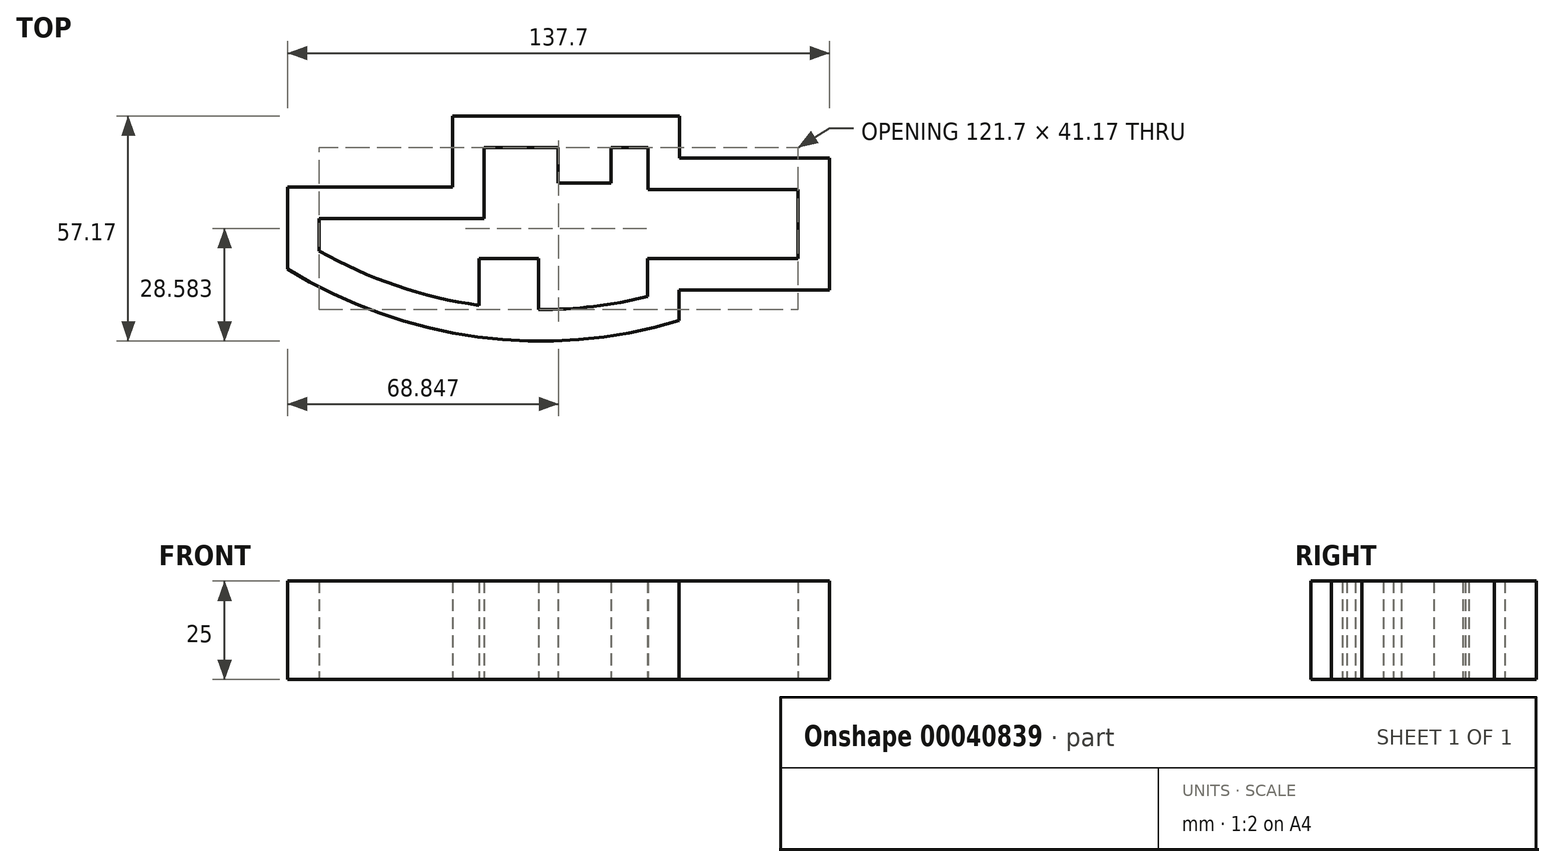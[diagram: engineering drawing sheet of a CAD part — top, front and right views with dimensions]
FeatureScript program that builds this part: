
annotation { "Feature Type Name" : "Feature", "Feature Type Description" : "" }
export const myFeature = defineFeature(function(context is Context, id is Id, definition is map)
    precondition{}
    {
        {
            var Q0;
            Q0=qCreatedBy(makeId("Top.planeOp"),FACE);
            var sketch = newSketch(context, id + "F0", { "sketchPlane" : qUnion([Q0])});
            skLineSegment(sketch, "E0", {"start": v(-50.92, 1.99) * mm, "end": v(-50.92, 10.24) * mm});
            skLineSegment(sketch, "E1", {"start": v(-50.92, 10.24) * mm, "end": v(-9.06, 10.24) * mm});
            skLineSegment(sketch, "E2", {"start": v(-9.06, 10.24) * mm, "end": v(-9.06, 28.27) * mm});
            skLineSegment(sketch, "E3", {"start": v(-9.06, 28.27) * mm, "end": v(9.73, 28.27) * mm});
            skLineSegment(sketch, "E4", {"start": v(32.61, 28.27) * mm, "end": v(32.61, 17.6) * mm});
            skLineSegment(sketch, "E5", {"start": v(32.61, 17.6) * mm, "end": v(70.78, 17.6) * mm});
            skLineSegment(sketch, "E6", {"start": v(70.78, 17.6) * mm, "end": v(70.78, 0) * mm});
            skLineSegment(sketch, "E7", {"start": v(70.78, 0) * mm, "end": v(32.48, 0) * mm});
            skLineSegment(sketch, "E8", {"start": v(32.48, 0) * mm, "end": v(32.48, -9.6) * mm});
            skArc(sketch, "E9", {"start": v(-50.92, 1.99) * mm, "mid": v(-31.29, -6.85) * mm, "end": v(-10.33, -11.82) * mm});
            skLineSegment(sketch, "E10.0", {"start": v(40.61, 36.27) * mm, "end": v(40.61, 25.6) * mm});
            skLineSegment(sketch, "E10.1", {"start": v(-17.06, 36.27) * mm, "end": v(40.61, 36.27) * mm});
            skLineSegment(sketch, "E10.2", {"start": v(40.61, 25.6) * mm, "end": v(78.78, 25.6) * mm});
            skLineSegment(sketch, "E10.3", {"start": v(-17.06, 18.24) * mm, "end": v(-17.06, 36.27) * mm});
            skLineSegment(sketch, "E10.4", {"start": v(-58.92, 18.24) * mm, "end": v(-17.06, 18.24) * mm});
            skLineSegment(sketch, "E10.5", {"start": v(-58.92, -2.56) * mm, "end": v(-58.92, 18.24) * mm});
            skLineSegment(sketch, "E10.6", {"start": v(78.78, 25.6) * mm, "end": v(78.78, -8) * mm});
            skLineSegment(sketch, "E10.7", {"start": v(78.78, -8) * mm, "end": v(40.48, -8) * mm});
            skLineSegment(sketch, "E10.8", {"start": v(40.48, -8) * mm, "end": v(40.48, -15.7) * mm});
            skArc(sketch, "E10.9", {"start": v(-58.92, -2.56) * mm, "mid": v(-10.64, -19.85) * mm, "end": v(40.48, -15.7) * mm});
            skLineSegment(sketch, "E11", {"start": v(9.73, 28.27) * mm, "end": v(9.73, 19.17) * mm});
            skLineSegment(sketch, "E12", {"start": v(9.73, 19.17) * mm, "end": v(23.3, 19.17) * mm});
            skLineSegment(sketch, "E13", {"start": v(23.3, 19.17) * mm, "end": v(23.3, 28.27) * mm});
            skLineSegment(sketch, "E14", {"start": v(-10.33, -11.82) * mm, "end": v(-10.33, 0) * mm});
            skLineSegment(sketch, "E15", {"start": v(-10.33, 0) * mm, "end": v(4.88, 0) * mm});
            skLineSegment(sketch, "E16", {"start": v(4.88, 0) * mm, "end": v(4.88, -12.9) * mm});
            skLineSegment(sketch, "E17.trimOffspring", {"start": v(23.3, 28.27) * mm, "end": v(32.61, 28.27) * mm});
            skArc(sketch, "E18.trimOffspring", {"start": v(4.88, -12.9) * mm, "mid": v(18.78, -12.1) * mm, "end": v(32.48, -9.6) * mm});
            skSolve(sketch);
        }
        {
            var Q0;
            Q0 = qSketchRegion(id + "F0", true);
            extrude(context, id + "F1", {"entities" : qUnion([Q0]), "depth" : 25 * mm});
        }
    });
